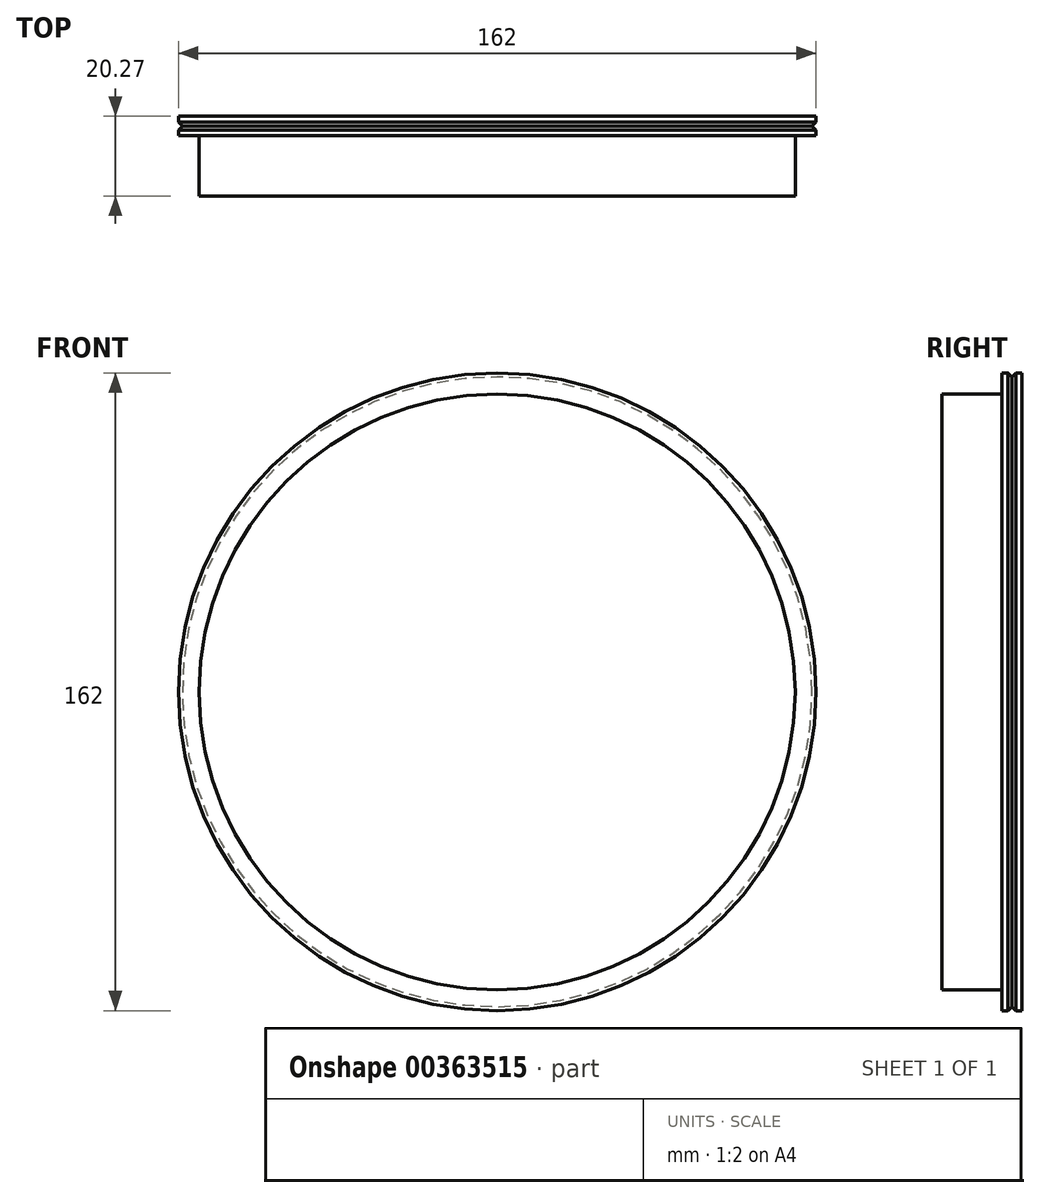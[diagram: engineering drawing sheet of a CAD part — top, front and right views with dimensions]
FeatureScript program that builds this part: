
annotation { "Feature Type Name" : "Feature", "Feature Type Description" : "" }
export const myFeature = defineFeature(function(context is Context, id is Id, definition is map)
    precondition{}
    {
        {
            var Q0;
            Q0=qCreatedBy(makeId("Right.planeOp"),FACE);
            var sketch = newSketch(context, id + "F0", { "sketchPlane" : qUnion([Q0])});
            skLineSegment(sketch, "E0", {"start": v(110.86, 0) * mm, "end": v(-109.14, 0) * mm, "construction": true});
            skLineSegment(sketch, "E1", {"start": v(0, 0) * mm, "end": v(0, 81) * mm});
            skLineSegment(sketch, "E2", {"start": v(0, 81) * mm, "end": v(-1.5, 81) * mm});
            skLineSegment(sketch, "E3", {"start": v(-1.5, 81) * mm, "end": v(-2.5, 80) * mm});
            skLineSegment(sketch, "E4", {"start": v(-2.5, 80) * mm, "end": v(-3.5, 81) * mm});
            skLineSegment(sketch, "E5", {"start": v(-3.5, 81) * mm, "end": v(-5, 81) * mm});
            skLineSegment(sketch, "E6", {"start": v(-5, 81) * mm, "end": v(-5, 75.7) * mm});
            skLineSegment(sketch, "E7", {"start": v(-5, 75.7) * mm, "end": v(-20.27, 75.7) * mm});
            skLineSegment(sketch, "E8", {"start": v(-20.27, 75.7) * mm, "end": v(-20.27, 0) * mm});
            skLineSegment(sketch, "E9", {"start": v(-20.27, 0) * mm, "end": v(0, 0) * mm});
            skSolve(sketch);
        }
        {
            var Q0;
            Q0 = qSketchRegion(id + "F0", true);
            var Q1;
            Q1=sQuery(id+"F0.wireOp",EDGE,"E0");
            revolve(context, id + "F1", {"entities" : qUnion([Q0]), "axis" : qUnion([Q1]), "revolveType" : RevolveType.FULL});
        }
    });
